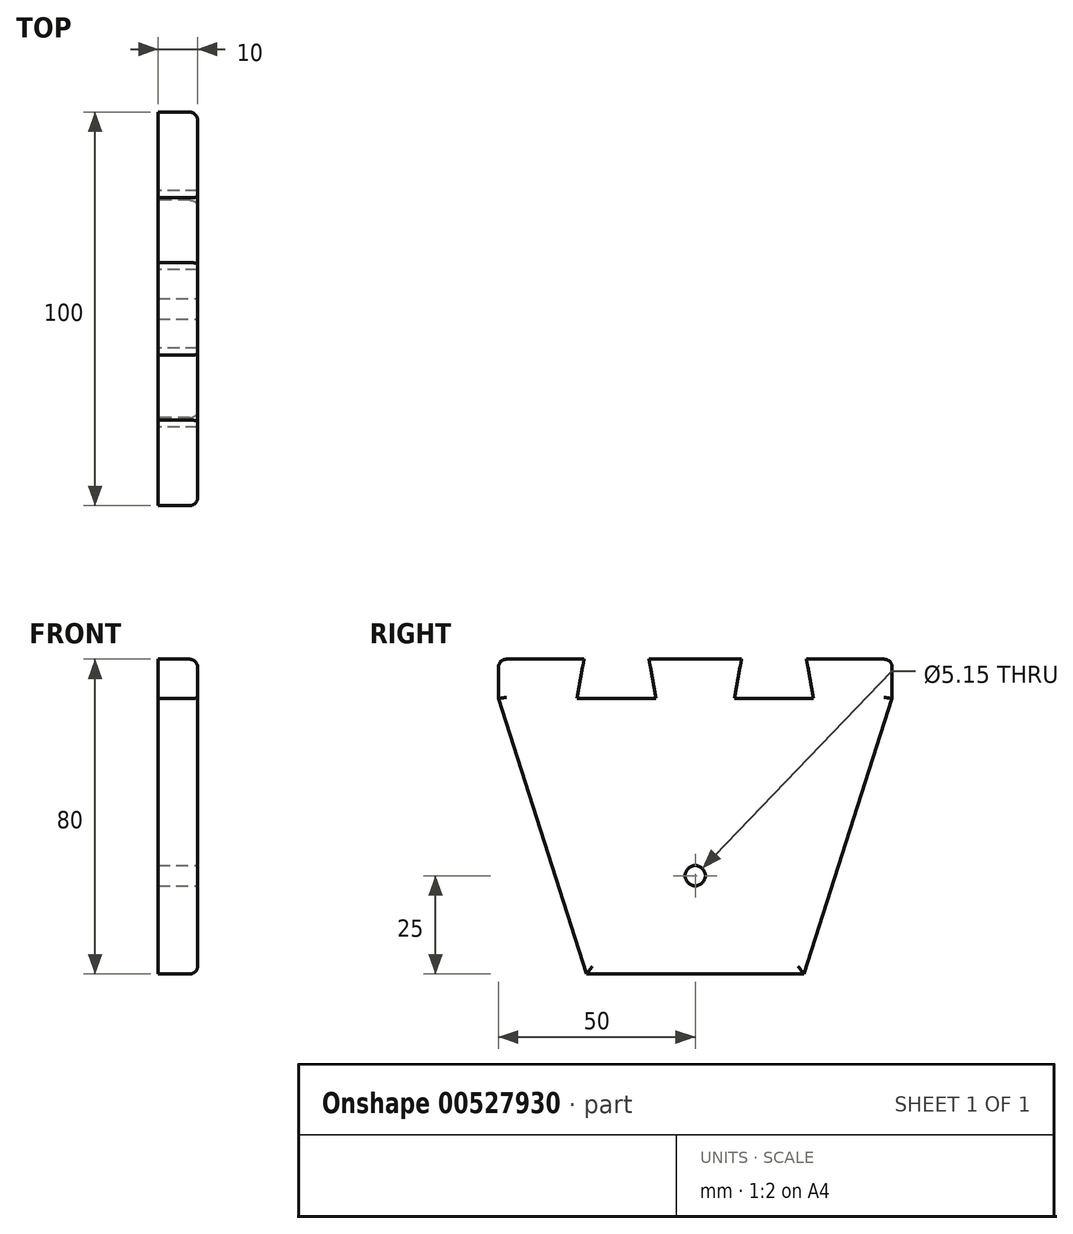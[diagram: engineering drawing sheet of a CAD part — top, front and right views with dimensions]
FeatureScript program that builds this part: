
annotation { "Feature Type Name" : "Feature", "Feature Type Description" : "" }
export const myFeature = defineFeature(function(context is Context, id is Id, definition is map)
    precondition{}
    {
        {
            var Q0;
            Q0=qCreatedBy(makeId("Right.planeOp"),FACE);
            var sketch = newSketch(context, id + "F0", { "sketchPlane" : qUnion([Q0])});
            skLineSegment(sketch, "E0", {"start": v(0, -70) * mm, "end": v(-27.6, -70) * mm});
            skLineSegment(sketch, "E1", {"start": v(-27.6, -70) * mm, "end": v(-50, 0) * mm});
            skLineSegment(sketch, "E2", {"start": v(-50, 0) * mm, "end": v(-50, 10) * mm});
            skLineSegment(sketch, "E3", {"start": v(-50, 10) * mm, "end": v(-28.24, 10) * mm});
            skLineSegment(sketch, "E4.MirrorCS", {"start": v(50, 10) * mm, "end": v(28.24, 10) * mm});
            skLineSegment(sketch, "E5.MirrorCS", {"start": v(50, 0) * mm, "end": v(50, 10) * mm});
            skLineSegment(sketch, "E6.MirrorCS", {"start": v(27.6, -70) * mm, "end": v(50, 0) * mm});
            skLineSegment(sketch, "E7.MirrorCS", {"start": v(0, -70) * mm, "end": v(27.6, -70) * mm});
            skLineSegment(sketch, "E8", {"start": v(-28.24, 10) * mm, "end": v(-30, 0) * mm});
            skLineSegment(sketch, "E9", {"start": v(-30, 0) * mm, "end": v(-20, 0) * mm});
            skLineSegment(sketch, "E10", {"start": v(-20, 0) * mm, "end": v(-20, 10) * mm, "construction": true});
            skLineSegment(sketch, "E11.MirrorCS", {"start": v(-11.76, 10) * mm, "end": v(-10, 0) * mm});
            skLineSegment(sketch, "E12.MirrorCS", {"start": v(-10, 0) * mm, "end": v(-20, 0) * mm});
            skLineSegment(sketch, "E13.MirrorCS", {"start": v(11.76, 10) * mm, "end": v(10, 0) * mm});
            skLineSegment(sketch, "E14.MirrorCS", {"start": v(10, 0) * mm, "end": v(20, 0) * mm});
            skLineSegment(sketch, "E15.MirrorCS", {"start": v(30, 0) * mm, "end": v(20, 0) * mm});
            skLineSegment(sketch, "E16.MirrorCS", {"start": v(28.24, 10) * mm, "end": v(30, 0) * mm});
            skLineSegment(sketch, "E17.trimOffspring", {"start": v(-11.76, 10) * mm, "end": v(0, 10) * mm});
            skLineSegment(sketch, "E18.trimOffspring", {"start": v(11.76, 10) * mm, "end": v(0, 10) * mm});
            skSolve(sketch);
        }
        {
            var Q0;
            Q0=makeQuery(id+"F0.imprint","IMPRINT",FACE,{"disambiguationData":[TD([[makeQuery(id+"F0.imprint","IMPRINT",EDGE,{"derivedFrom":sQuery(id+"F0.wireOp",EDGE,"E0")}),-1.0]])]});
            extrude(context, id + "F1", {"entities" : qUnion([Q0]), "depth" : 10 * mm, "offsetDistance" : 25 * mm});
        }
        {
            var Q0;
            Q0=makeQuery(id+"F1.opExtrude","CAP_FACE",FACE,{"disambiguationData":[OSD([sQuery(id+"F0.wireOp",EDGE,"E0"),sQuery(id+"F0.wireOp",EDGE,"E1"),sQuery(id+"F0.wireOp",EDGE,"E2"),sQuery(id+"F0.wireOp",EDGE,"E3"),sQuery(id+"F0.wireOp",EDGE,"E4.MirrorCS"),sQuery(id+"F0.wireOp",EDGE,"E5.MirrorCS"),sQuery(id+"F0.wireOp",EDGE,"E6.MirrorCS"),sQuery(id+"F0.wireOp",EDGE,"E7.MirrorCS"),sQuery(id+"F0.wireOp",EDGE,"E8"),sQuery(id+"F0.wireOp",EDGE,"E9"),sQuery(id+"F0.wireOp",EDGE,"E11.MirrorCS"),sQuery(id+"F0.wireOp",EDGE,"E12.MirrorCS"),sQuery(id+"F0.wireOp",EDGE,"E13.MirrorCS"),sQuery(id+"F0.wireOp",EDGE,"E14.MirrorCS"),sQuery(id+"F0.wireOp",EDGE,"E15.MirrorCS"),sQuery(id+"F0.wireOp",EDGE,"E16.MirrorCS"),sQuery(id+"F0.wireOp",EDGE,"E17.trimOffspring"),sQuery(id+"F0.wireOp",EDGE,"E18.trimOffspring")])],"isStart":false});
            var sketch = newSketch(context, id + "F2", { "sketchPlane" : qUnion([Q0])});
            skCircle(sketch, "E19", {"center": v(0, -45) * mm, "radius": 2.58 * mm});
            skLineSegment(sketch, "E20.0.0", {"start": v(50, 0) * mm, "end": v(50, 10) * mm});
            skLineSegment(sketch, "E20.0.1", {"start": v(50, 10) * mm, "end": v(28.24, 10) * mm});
            skLineSegment(sketch, "E20.0.2", {"start": v(28.24, 10) * mm, "end": v(30, 0) * mm});
            skLineSegment(sketch, "E20.0.3", {"start": v(30, 0) * mm, "end": v(10, 0) * mm});
            skLineSegment(sketch, "E20.0.4", {"start": v(10, 0) * mm, "end": v(11.76, 10) * mm});
            skLineSegment(sketch, "E20.0.5", {"start": v(11.76, 10) * mm, "end": v(-11.76, 10) * mm});
            skLineSegment(sketch, "E20.0.6", {"start": v(-11.76, 10) * mm, "end": v(-10, 0) * mm});
            skLineSegment(sketch, "E20.0.7", {"start": v(-10, 0) * mm, "end": v(-30, 0) * mm});
            skLineSegment(sketch, "E20.0.8", {"start": v(-30, 0) * mm, "end": v(-28.24, 10) * mm});
            skLineSegment(sketch, "E20.0.9", {"start": v(-28.24, 10) * mm, "end": v(-50, 10) * mm});
            skLineSegment(sketch, "E20.0.10", {"start": v(-50, 10) * mm, "end": v(-50, 0) * mm});
            skLineSegment(sketch, "E20.0.11", {"start": v(-50, 0) * mm, "end": v(-27.6, -70) * mm});
            skLineSegment(sketch, "E20.0.12", {"start": v(-27.6, -70) * mm, "end": v(27.6, -70) * mm});
            skLineSegment(sketch, "E20.0.13", {"start": v(27.6, -70) * mm, "end": v(50, 0) * mm});
            skSolve(sketch);
        }
        {
            var Q0;
            Q0=makeQuery(id+"F2.imprint","IMPRINT",FACE,{"disambiguationData":[TD([[makeQuery(id+"F2.imprint","IMPRINT",EDGE,{"derivedFrom":sQuery(id+"F2.wireOp",EDGE,"E19")}),1.0]])]});
            extrude(context, id + "F3", {"entities" : qUnion([Q0]), "operationType" : NewBodyOperationType.REMOVE, "endBound" : BoundingType.UP_TO_NEXT, "oppositeDirection" : true, "depth" : 25 * mm, "offsetDistance" : 25 * mm});
        }
        {
            var Q0;
            Q0=makeQuery(id+"F1.opExtrude","SWEPT_EDGE",EDGE,{"disambiguationData":[OSD([sQuery(id+"F0.wireOp",EDGE,"E2"),sQuery(id+"F0.wireOp",EDGE,"E3")])]});
            var Q1;
            Q1=makeQuery(id+"F1.opExtrude","SWEPT_EDGE",EDGE,{"disambiguationData":[OSD([sQuery(id+"F0.wireOp",EDGE,"E4.MirrorCS"),sQuery(id+"F0.wireOp",EDGE,"E5.MirrorCS")])]});
            var Q2;
            Q2=makeQuery(id+"F1.opExtrude","CAP_EDGE",EDGE,{"disambiguationData":[OSD([sQuery(id+"F0.wireOp",EDGE,"E3")])],"isStart":false});
            var Q3;
            Q3=makeQuery(id+"F1.opExtrude","CAP_EDGE",EDGE,{"disambiguationData":[OSD([sQuery(id+"F0.wireOp",EDGE,"E17.trimOffspring"),sQuery(id+"F0.wireOp",EDGE,"E18.trimOffspring")])],"isStart":false});
            var Q4;
            Q4=makeQuery(id+"F1.opExtrude","CAP_EDGE",EDGE,{"disambiguationData":[OSD([sQuery(id+"F0.wireOp",EDGE,"E4.MirrorCS")])],"isStart":false});
            var Q5;
            Q5=makeQuery(id+"F1.opExtrude","CAP_EDGE",EDGE,{"disambiguationData":[OSD([sQuery(id+"F0.wireOp",EDGE,"E2")])],"isStart":false});
            var Q6;
            Q6=makeQuery(id+"F1.opExtrude","CAP_EDGE",EDGE,{"disambiguationData":[OSD([sQuery(id+"F0.wireOp",EDGE,"E1")])],"isStart":false});
            var Q7;
            Q7=makeQuery(id+"F1.opExtrude","CAP_EDGE",EDGE,{"disambiguationData":[OSD([sQuery(id+"F0.wireOp",EDGE,"E6.MirrorCS")])],"isStart":false});
            var Q8;
            Q8=makeQuery(id+"F1.opExtrude","CAP_EDGE",EDGE,{"disambiguationData":[OSD([sQuery(id+"F0.wireOp",EDGE,"E5.MirrorCS")])],"isStart":false});
            var Q9;
            Q9=makeQuery(id+"F1.opExtrude","CAP_EDGE",EDGE,{"disambiguationData":[OSD([sQuery(id+"F0.wireOp",EDGE,"E0"),sQuery(id+"F0.wireOp",EDGE,"E7.MirrorCS")])],"isStart":false});
            fillet(context, id + "F4", {"entities" : qUnion([Q0, Q1, Q2, Q3, Q4, Q5, Q6, Q7, Q8, Q9]), "radius" : 2 * mm, "tangentPropagation" : true, "allowEdgeOverflow" : false});
        }
    });
